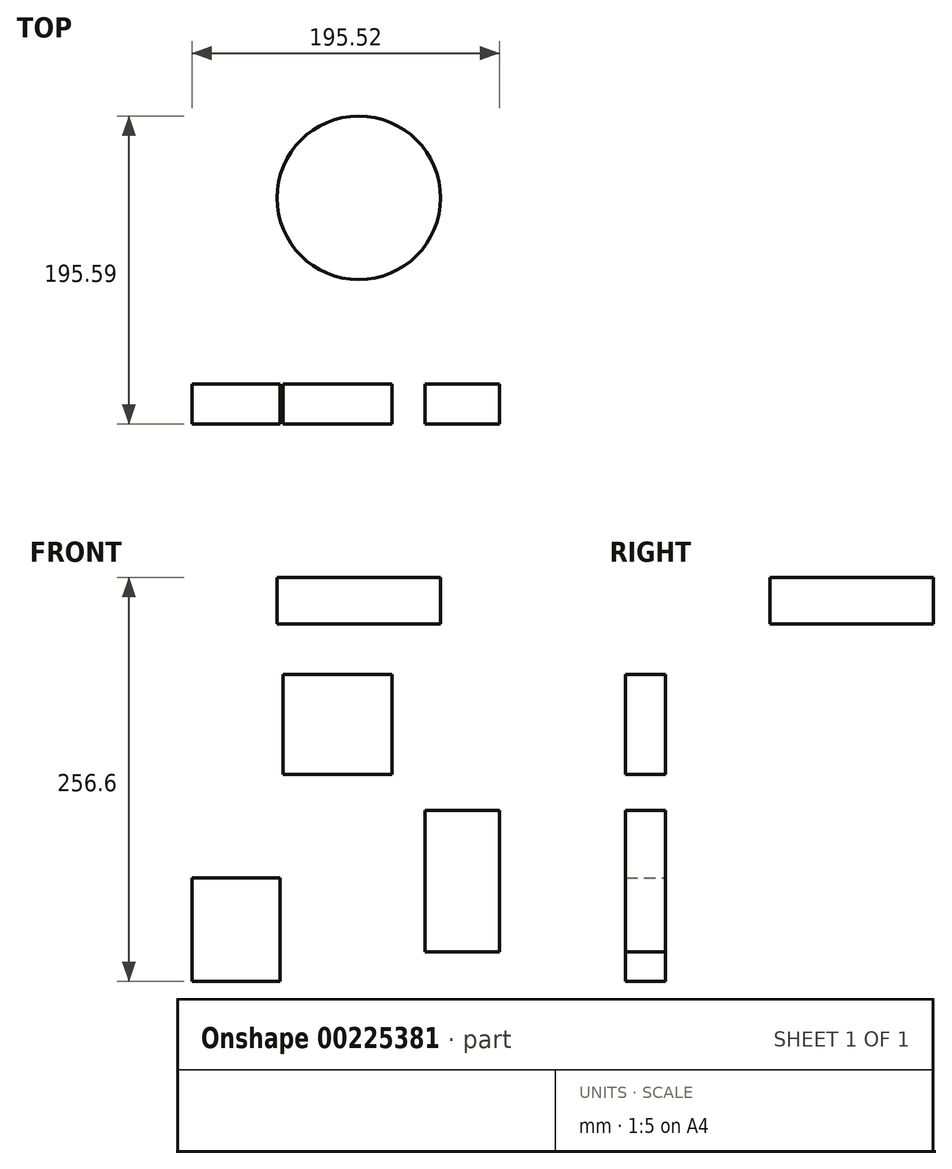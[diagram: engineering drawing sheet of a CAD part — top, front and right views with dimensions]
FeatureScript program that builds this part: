
annotation { "Feature Type Name" : "Feature", "Feature Type Description" : "" }
export const myFeature = defineFeature(function(context is Context, id is Id, definition is map)
    precondition{}
    {
        {
            var Q0;
            Q0=qCreatedBy(makeId("Front.planeOp"),FACE);
            var sketch = newSketch(context, id + "F0", { "sketchPlane" : qUnion([Q0])});
            skLineSegment(sketch, "E0.bottom", {"start": v(-48, 100.66) * mm, "end": v(21, 100.66) * mm});
            skLineSegment(sketch, "E0.top", {"start": v(-48, 37.07) * mm, "end": v(21, 37.07) * mm});
            skLineSegment(sketch, "E0.left", {"start": v(-48, 100.66) * mm, "end": v(-48, 37.07) * mm});
            skLineSegment(sketch, "E0.right", {"start": v(21, 100.66) * mm, "end": v(21, 37.07) * mm});
            skLineSegment(sketch, "E1.bottom", {"start": v(-106.01, -28.6) * mm, "end": v(-50, -28.6) * mm});
            skLineSegment(sketch, "E1.top", {"start": v(-106.01, -94.45) * mm, "end": v(-50, -94.45) * mm});
            skLineSegment(sketch, "E1.left", {"start": v(-106.01, -28.6) * mm, "end": v(-106.01, -94.45) * mm});
            skLineSegment(sketch, "E1.right", {"start": v(-50, -28.6) * mm, "end": v(-50, -94.45) * mm});
            skLineSegment(sketch, "E2.bottom", {"start": v(42, 14.13) * mm, "end": v(89.51, 14.13) * mm});
            skLineSegment(sketch, "E2.top", {"start": v(42, -75.67) * mm, "end": v(89.51, -75.67) * mm});
            skLineSegment(sketch, "E2.left", {"start": v(42, 14.13) * mm, "end": v(42, -75.67) * mm});
            skLineSegment(sketch, "E2.right", {"start": v(89.51, 14.13) * mm, "end": v(89.51, -75.67) * mm});
            skSolve(sketch);
        }
        {
            var Q0;
            Q0=qSketchRegion(id+"F0",true);
            extrude(context, id + "F1", {"entities" : qUnion([Q0]), "depth" : 25.4 * mm});
        }
        {
            var Q0;
            Q0=qCreatedBy(makeId("Right.planeOp"),FACE);
            var sketch = newSketch(context, id + "F2", { "sketchPlane" : qUnion([Q0])});
            skLineSegment(sketch, "E3.bottom", {"start": v(118.24, 162.15) * mm, "end": v(170.19, 162.15) * mm});
            skLineSegment(sketch, "E3.top", {"start": v(118.24, 132.77) * mm, "end": v(170.19, 132.77) * mm});
            skLineSegment(sketch, "E3.left", {"start": v(118.24, 162.15) * mm, "end": v(118.24, 132.77) * mm});
            skLineSegment(sketch, "E3.right", {"start": v(170.19, 162.15) * mm, "end": v(170.19, 132.77) * mm});
            skSolve(sketch);
        }
        {
            var Q0;
            Q0=qSketchRegion(id+"F2",true);
            var Q1;
            Q1=sQuery(id+"F2.wireOp",EDGE,"E3.left");
            revolve(context, id + "F3", {"entities" : qUnion([Q0]), "axis" : qUnion([Q1]), "revolveType" : RevolveType.FULL});
        }
    });
